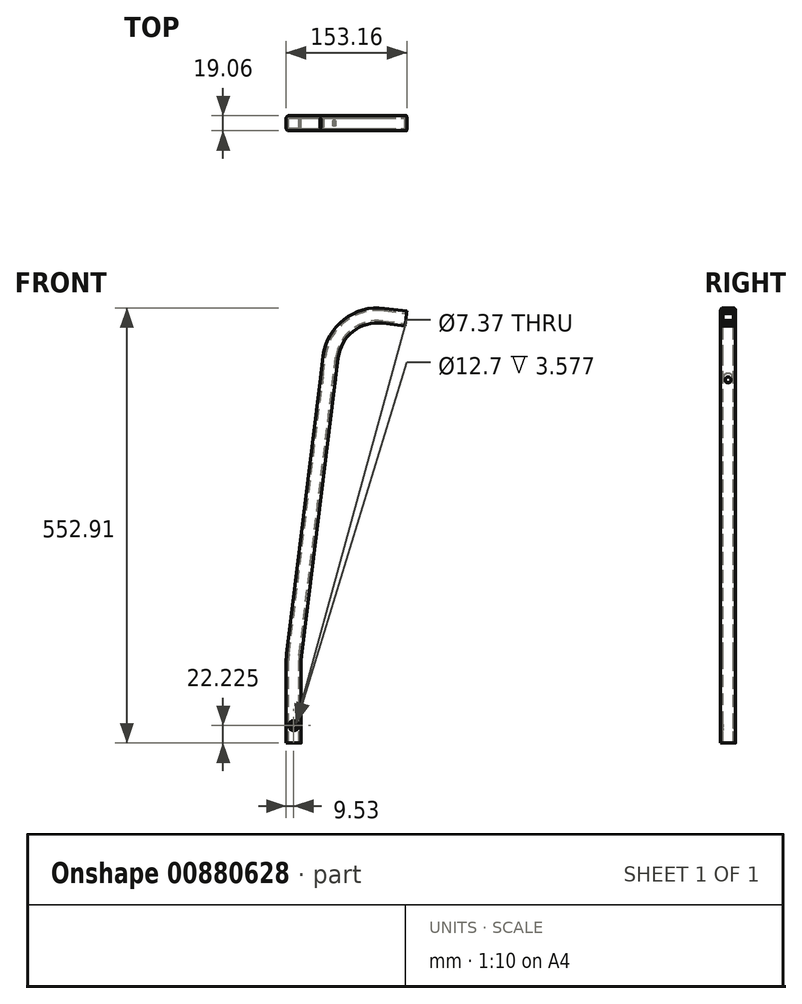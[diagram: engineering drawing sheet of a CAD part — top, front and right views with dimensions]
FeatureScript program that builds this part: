
annotation { "Feature Type Name" : "Feature", "Feature Type Description" : "" }
export const myFeature = defineFeature(function(context is Context, id is Id, definition is map)
    precondition{}
    {
        {
            var Q0;
            Q0=qCreatedBy(makeId("Front.planeOp"),FACE);
            var sketch = newSketch(context, id + "F0", { "sketchPlane" : qUnion([Q0])});
            skLineSegment(sketch, "E0", {"start": v(0, 0) * mm, "end": v(0, 104.9) * mm});
            skLineSegment(sketch, "E1", {"start": v(0.45, 112.25) * mm, "end": v(46.88, 490.41) * mm});
            skLineSegment(sketch, "E2", {"start": v(114.1, 542.94) * mm, "end": v(117.9, 542.47) * mm});
            skArc(sketch, "E3.filletArc", {"start": v(114.1, 542.94) * mm, "mid": v(69.62, 530.6) * mm, "end": v(46.88, 490.41) * mm});
            skPoint(sketch, "E4.visualSharp", {"position": v(0, 108.6) * mm});
            skArc(sketch, "E5.filletArc", {"start": v(0.45, 112.25) * mm, "mid": v(0.11, 108.58) * mm, "end": v(0, 104.9) * mm});
            skSolve(sketch);
        }
        {
            var Q0;
            Q0=qCreatedBy(makeId("Top.planeOp"),FACE);
            var sketch = newSketch(context, id + "F1", { "sketchPlane" : qUnion([Q0])});
            skLineSegment(sketch, "E6.bottom", {"start": v(-6.35, -9.52) * mm, "end": v(6.35, -9.53) * mm});
            skLineSegment(sketch, "E6.top", {"start": v(-6.35, 9.53) * mm, "end": v(6.35, 9.52) * mm});
            skLineSegment(sketch, "E6.left", {"start": v(-9.53, -6.35) * mm, "end": v(-9.52, 6.35) * mm});
            skLineSegment(sketch, "E6.right", {"start": v(9.53, -6.35) * mm, "end": v(9.53, 6.35) * mm});
            skLineSegment(sketch, "E7", {"start": v(0, -9.53) * mm, "end": v(0, 9.53) * mm, "construction": true});
            skPoint(sketch, "E7.startSnap0", {"position": v(0, -9.53) * mm});
            skLineSegment(sketch, "E8", {"start": v(-9.53, 0) * mm, "end": v(9.53, 0) * mm, "construction": true});
            skLineSegment(sketch, "E9.0", {"start": v(-5.46, -6.48) * mm, "end": v(5.46, -6.48) * mm});
            skLineSegment(sketch, "E9.1", {"start": v(-6.48, -5.46) * mm, "end": v(-6.48, 5.46) * mm});
            skLineSegment(sketch, "E9.2", {"start": v(-5.46, 6.48) * mm, "end": v(5.46, 6.48) * mm});
            skLineSegment(sketch, "E9.3", {"start": v(6.48, -5.46) * mm, "end": v(6.48, 5.46) * mm});
            skPoint(sketch, "E10.visualSharp", {"position": v(-6.48, 6.48) * mm});
            skArc(sketch, "E10.filletArc", {"start": v(-5.46, 6.48) * mm, "mid": v(-6.18, 6.18) * mm, "end": v(-6.48, 5.46) * mm});
            skPoint(sketch, "E11.visualSharp", {"position": v(6.48, 6.48) * mm});
            skArc(sketch, "E11.filletArc", {"start": v(6.48, 5.46) * mm, "mid": v(6.18, 6.18) * mm, "end": v(5.46, 6.48) * mm});
            skPoint(sketch, "E12.visualSharp", {"position": v(6.48, -6.48) * mm});
            skArc(sketch, "E12.filletArc", {"start": v(5.46, -6.48) * mm, "mid": v(6.18, -6.18) * mm, "end": v(6.48, -5.46) * mm});
            skPoint(sketch, "E13.visualSharp", {"position": v(-6.48, -6.48) * mm});
            skArc(sketch, "E13.filletArc", {"start": v(-6.48, -5.46) * mm, "mid": v(-6.18, -6.18) * mm, "end": v(-5.46, -6.48) * mm});
            skPoint(sketch, "E14.visualSharp", {"position": v(9.53, -9.53) * mm});
            skArc(sketch, "E14.filletArc", {"start": v(6.35, -9.53) * mm, "mid": v(8.6, -8.6) * mm, "end": v(9.53, -6.35) * mm});
            skPoint(sketch, "E15.visualSharp", {"position": v(-9.53, -9.52) * mm});
            skArc(sketch, "E15.filletArc", {"start": v(-9.52, -6.35) * mm, "mid": v(-8.6, -8.6) * mm, "end": v(-6.35, -9.52) * mm});
            skPoint(sketch, "E16.visualSharp", {"position": v(-9.53, 9.53) * mm});
            skArc(sketch, "E16.filletArc", {"start": v(-6.35, 9.53) * mm, "mid": v(-8.6, 8.6) * mm, "end": v(-9.53, 6.35) * mm});
            skPoint(sketch, "E17.visualSharp", {"position": v(9.53, 9.52) * mm});
            skArc(sketch, "E17.filletArc", {"start": v(9.53, 6.35) * mm, "mid": v(8.6, 8.6) * mm, "end": v(6.35, 9.52) * mm});
            skSolve(sketch);
        }
        {
            var Q0;
            Q0=makeQuery(id+"F1.imprint","IMPRINT",FACE,{"disambiguationData":[TD([[makeQuery(id+"F1.imprint","IMPRINT",EDGE,{"derivedFrom":sQuery(id+"F1.wireOp",EDGE,"uXW7z18t-WP6T-WkQb-FE9L-uBb2vWNNibH4")}),1.0]])]});
            var Q1;
            Q1=makeQuery(id+"F1.imprint","IMPRINT",FACE,{"disambiguationData":[TD([[makeQuery(id+"F1.imprint","IMPRINT",EDGE,{"derivedFrom":sQuery(id+"F1.wireOp",EDGE,"E6.bottom")}),1.0]])]});
            var Q2;
            Q2=sQuery(id+"F0.wireOp",EDGE,"E0");
            var Q3;
            Q3=sQuery(id+"F0.wireOp",EDGE,"E5.filletArc");
            var Q4;
            Q4=sQuery(id+"F0.wireOp",EDGE,"E1");
            var Q5;
            Q5=sQuery(id+"F0.wireOp",EDGE,"E3.filletArc");
            var Q6;
            Q6=sQuery(id+"F0.wireOp",EDGE,"E2");
            sweep(context, id + "F2", {"profiles" : qUnion([Q0, Q1]), "path" : qUnion([Q2, Q3, Q4, Q5, Q6])});
        }
        {
            var Q0;
            Q0=sQuery(id+"F0.wireOp",EDGE,"E2");
            cPlane(context, id + "F3", {"entities" : qUnion([Q0]), "cplaneType" : CPlaneType.LINE_ANGLE, "offset" : 25.4 * mm, "angle" : 90 * degree, "width" : 152.4 * mm, "height" : 152.4 * mm});
        }
        {
            var Q0;
            Q0=qCreatedBy(makeId("Front.planeOp"),FACE);
            var sketch = newSketch(context, id + "F4", { "sketchPlane" : qUnion([Q0])});
            skCircle(sketch, "E18", {"center": v(0, 22.23) * mm, "radius": 3.68 * mm});
            skSolve(sketch);
        }
        {
            var Q0;
            Q0=qSketchRegion(id+"F4",true);
            extrude(context, id + "F5", {"entities" : qUnion([Q0]), "operationType" : NewBodyOperationType.REMOVE, "endBound" : BoundingType.SYMMETRIC, "oppositeDirection" : true, "depth" : 668.02 * mm});
        }
        {
            var Q0;
            Q0=makeQuery(id+"F2.opSweep","SWEPT_FACE",FACE,{"disambiguationData":[OSD([sQuery(id+"F0.wireOp",EDGE,"E1"),sQuery(id+"F1.wireOp",EDGE,"E6.left")])]});
            var sketch = newSketch(context, id + "F6", { "sketchPlane" : qUnion([Q0])});
            skCircle(sketch, "E19", {"center": v(0, 464.53) * mm, "radius": 3.68 * mm});
            skSolve(sketch);
        }
        {
            var Q0;
            Q0 = qSketchRegion(id + "F6", true);
            extrude(context, id + "F7", {"entities" : qUnion([Q0]), "operationType" : NewBodyOperationType.REMOVE, "oppositeDirection" : true, "depth" : 25.4 * mm, "offsetDistance" : 25.4 * mm});
        }
        {
            var Q0;
            Q0=makeQuery(id+"F2.opSweep","SWEPT_FACE",FACE,{"disambiguationData":[OSD([sQuery(id+"F0.wireOp",EDGE,"E1"),sQuery(id+"F1.wireOp",EDGE,"E6.left")])]});
            var sketch = newSketch(context, id + "F8", { "sketchPlane" : qUnion([Q0])});
            skCircle(sketch, "E20", {"center": v(0, 464.53) * mm, "radius": 6.35 * mm});
            skSolve(sketch);
        }
        {
            var Q0;
            Q0 = qSketchRegion(id + "F8", true);
            extrude(context, id + "F9", {"entities" : qUnion([Q0]), "operationType" : NewBodyOperationType.REMOVE, "oppositeDirection" : true, "depth" : 9.47 * mm, "offsetDistance" : 25.4 * mm});
        }
        {
            var Q0;
            Q0=makeQuery(id+"F2.opSweep","CAP_FACE",FACE,{"disambiguationData":[OSD([sQuery(id+"F0.wireOp",VERTEX,"E2.end"),sQuery(id+"F1.wireOp",EDGE,"E6.bottom"),sQuery(id+"F1.wireOp",EDGE,"E6.top"),sQuery(id+"F1.wireOp",EDGE,"E6.left"),sQuery(id+"F1.wireOp",EDGE,"E6.right"),sQuery(id+"F1.wireOp",EDGE,"E9.0"),sQuery(id+"F1.wireOp",EDGE,"E9.1"),sQuery(id+"F1.wireOp",EDGE,"E9.2"),sQuery(id+"F1.wireOp",EDGE,"E9.3")])],"isStart":false});
            var sketch = newSketch(context, id + "F10", { "sketchPlane" : qUnion([Q0])});
            skLineSegment(sketch, "E21.0", {"start": v(-5.46, 559.27) * mm, "end": v(5.46, 559.27) * mm});
            skArc(sketch, "E21.1", {"start": v(5.46, 559.27) * mm, "mid": v(6.18, 558.98) * mm, "end": v(6.48, 558.26) * mm});
            skLineSegment(sketch, "E21.2", {"start": v(6.48, 558.26) * mm, "end": v(6.48, 547.34) * mm});
            skArc(sketch, "E21.3", {"start": v(6.48, 547.34) * mm, "mid": v(6.18, 546.62) * mm, "end": v(5.46, 546.32) * mm});
            skLineSegment(sketch, "E21.4", {"start": v(5.46, 546.32) * mm, "end": v(-5.46, 546.32) * mm});
            skArc(sketch, "E21.5", {"start": v(-5.46, 546.32) * mm, "mid": v(-6.18, 546.62) * mm, "end": v(-6.48, 547.34) * mm});
            skLineSegment(sketch, "E21.6", {"start": v(-6.48, 547.34) * mm, "end": v(-6.48, 558.26) * mm});
            skArc(sketch, "E21.7", {"start": v(-6.48, 558.26) * mm, "mid": v(-6.18, 558.98) * mm, "end": v(-5.46, 559.27) * mm});
            skLineSegment(sketch, "E22.0", {"start": v(6.35, 562.32) * mm, "end": v(-6.35, 562.32) * mm});
            skArc(sketch, "E22.1", {"start": v(9.53, 559.15) * mm, "mid": v(8.6, 561.4) * mm, "end": v(6.35, 562.32) * mm});
            skLineSegment(sketch, "E22.2", {"start": v(9.53, 559.15) * mm, "end": v(9.52, 546.45) * mm});
            skArc(sketch, "E22.3", {"start": v(6.35, 543.27) * mm, "mid": v(8.6, 544.2) * mm, "end": v(9.53, 546.45) * mm});
            skLineSegment(sketch, "E22.4", {"start": v(-6.35, 543.27) * mm, "end": v(6.35, 543.27) * mm});
            skArc(sketch, "E22.5", {"start": v(-9.53, 546.45) * mm, "mid": v(-8.6, 544.2) * mm, "end": v(-6.35, 543.27) * mm});
            skLineSegment(sketch, "E22.6", {"start": v(-9.52, 559.15) * mm, "end": v(-9.53, 546.45) * mm});
            skArc(sketch, "E22.7", {"start": v(-6.35, 562.32) * mm, "mid": v(-8.6, 561.4) * mm, "end": v(-9.53, 559.15) * mm});
            skSolve(sketch);
        }
        {
            var Q0;
            Q0 = qSketchRegion(id + "F10", true);
            extrude(context, id + "F11", {"entities" : qUnion([Q0]), "operationType" : NewBodyOperationType.ADD, "depth" : 24.76 * mm, "offsetDistance" : 25.4 * mm});
        }
        {
            var Q0;
            Q0=makeQuery(id+"F11.boolean.opBoolean","MERGE",FACE,{"derivedFrom":[makeQuery(id+"F2.opSweep","SWEPT_FACE",FACE,{"disambiguationData":[OSD([sQuery(id+"F0.wireOp",EDGE,"E2"),sQuery(id+"F1.wireOp",EDGE,"E6.bottom")])]}),makeQuery(id+"F11.opExtrude","SWEPT_FACE",FACE,{"disambiguationData":[OSD([sQuery(id+"F10.wireOp",EDGE,"E22.6")])]})]});
            var sketch = newSketch(context, id + "F12", { "sketchPlane" : qUnion([Q0])});
            skCircle(sketch, "E23", {"center": v(0, 22.23) * mm, "radius": 6.35 * mm});
            skSolve(sketch);
        }
        {
            var Q0;
            Q0 = qSketchRegion(id + "F12", true);
            extrude(context, id + "F13", {"entities" : qUnion([Q0]), "operationType" : NewBodyOperationType.REMOVE, "oppositeDirection" : true, "depth" : 12.45 * mm, "offsetDistance" : 25.4 * mm});
        }
    });
